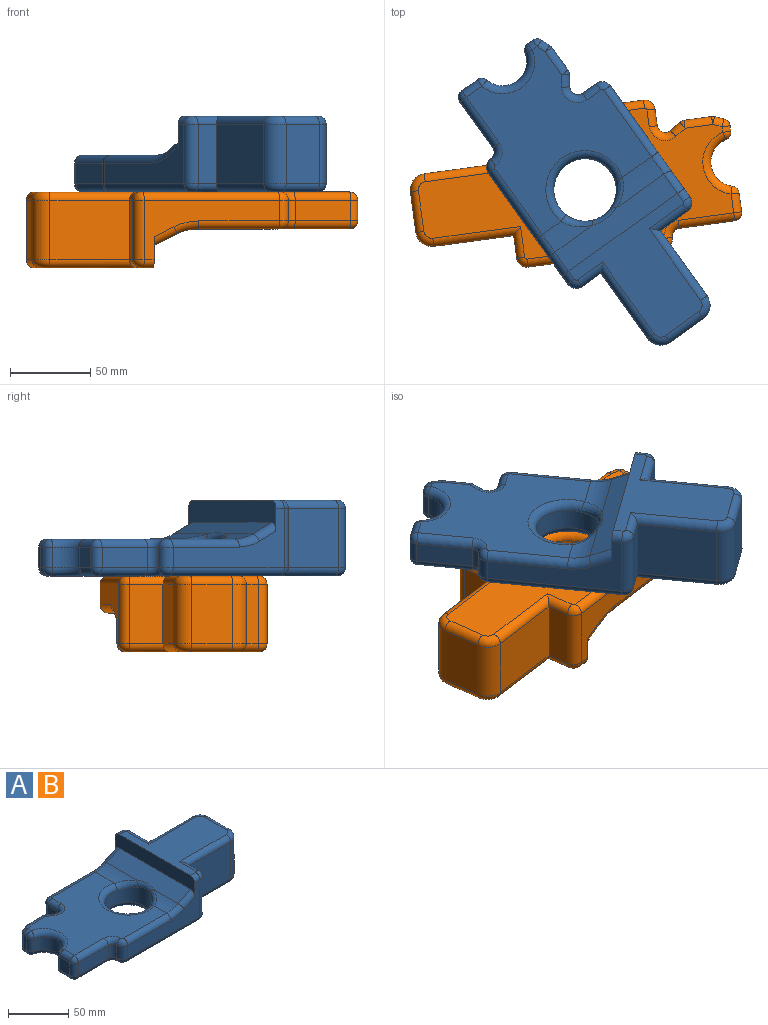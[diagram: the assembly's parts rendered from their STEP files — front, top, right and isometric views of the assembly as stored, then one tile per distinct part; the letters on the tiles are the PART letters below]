
ASSEMBLY  parts=2 mates=1
PART A: 109 faces, bbox 203.6x93.4x47.3 mm
  f0: cylinder r=30mm len=36.62mm, axis (0,-1,0), area 377.4mm2, adj f26,f28,f30,f66
  f1: cylinder r=30mm len=28.88mm, axis (0,-1,0), area 270.5mm2, adj f26,f28,f33,f44
  f2: plane 37.3x14.28mm, normal (1,0,0), area 532.7mm2, adj f3,f23,f76,f98
  f3: plane 50.1x37.3mm, normal (0,-1,0), area 1868.8mm2, adj f2,f4,f78,f96
  f4: cylinder r=10mm len=37.3mm, axis (0,0,-1), area 585.9mm2, adj f3,f5,f77,f94
  f5: plane 37.3x25.56mm, normal (1,0,0), area 953.5mm2, adj f4,f6,f75,f92
  f6: cylinder r=10mm len=37.3mm, axis (0,0,-1), area 585.9mm2, adj f5,f7,f73,f90
  f7: plane 50.1x37.3mm, normal (0,1,0), area 1868.8mm2, adj f6,f8,f71,f88
  f8: plane 37.3x20.87mm, normal (1,0,0), area 778.6mm2, adj f7,f9,f70,f86
  f9: cylinder r=6.35mm len=37.3mm, axis (0,0,-1), area 372.1mm2, adj f8,f10,f69,f84
  f10: plane 85.02x37.3mm, normal (0,1,0), area 1363.6mm2, adj f9,f11,f27,f65,f66,f67,f68,f82
  f11: cylinder r=6.35mm len=13.05mm, axis (0,0,-1), area 130.1mm2, adj f10,f12,f64,f80
  f12: plane 13.05x10.53mm, normal (-1,0,0), area 137.3mm2, adj f11,f35,f63,f79
  f13: plane 13.05x6.37mm, normal (0.57,0.82,0), area 100.7mm2, adj f35,f40,f61,f83
  f14: plane 17.3x13.05mm, normal (0,1,0), area 225.7mm2, adj f40,f41,f59,f87
  f15: plane 13.05x5.67mm, normal (-0.36,0.93,0), area 79.1mm2, adj f41,f42,f57,f91
  f16: plane 13.05x3.52mm, normal (-1,0,0), area 45.9mm2, adj f37,f42,f55,f95
  f17: cylinder r=15.04mm len=29.12mm, axis (0,0,-1), area 517.2mm2, adj f37,f38,f53,f99
  f18: plane 13.05x11.79mm, normal (-1,0,0), area 153.8mm2, adj f38,f39,f51,f103
  f19: plane 34.99x13.05mm, normal (0,-1,0), area 456.4mm2, adj f36,f39,f49,f107
  f20: plane 13.05x0.03mm, normal (-1,0,0), area 0.4mm2, adj f21,f36,f47,f106
  f21: cylinder r=6.35mm len=13.05mm, axis (0,0,-1), area 130.1mm2, adj f20,f22,f46,f104
  f22: plane 85.02x37.3mm, normal (0,-1,0), area 1363.6mm2, adj f21,f23,f27,f43,f44,f45,f72,f102
  f23: cylinder r=6.35mm len=37.3mm, axis (0,0,-1), area 372.1mm2, adj f2,f22,f74,f100
  f24: plane 83.42x67.73mm, normal (0,0,1), area 2762.3mm2, adj f27,f68,f69,f70,f71,f72,f73,f74
  f25: plane 192.81x83.42mm, normal (0,0,-1), area 9588.8mm2, adj f34,f79,f80,f81,f82,f83,f84,f86
  f26: plane 83.42x14.66mm, normal (-0.44,0,0.9), area 1342.7mm2, adj f0,f1,f27,f32,f43,f67
  f27: plane 93.42x19.43mm, normal (-1,0,0), area 1295.1mm2, adj f10,f22,f24,f26,f43,f67,f68,f72
  f28: plane 97.08x83.42mm, normal (0,0,1), area 5083.9mm2, adj f0,f1,f31,f45,f46,f47,f48,f49
  f29: cylinder r=19.49mm len=38.98mm, axis (0,0,-1), area 1710.3mm2, adj f30,f31,f32,f33,f34
  f30: bspline ~18.56x17.26mm, area 127.5mm2, adj f0,f29,f31,f32
  f31: torus R=24.49mm, axis (0,0,-1), area 625.9mm2, adj f28,f29,f30,f33
  f32: bspline ~17.93x5.32mm, area 91.8mm2, adj f26,f29,f30,f33
  f33: bspline ~18.06x17.1mm, area 127.5mm2, adj f1,f29,f31,f32
  f34: torus R=24.49mm, axis (0,0,1), area 1051.3mm2, adj f25,f29
  f35: cylinder r=5mm len=13.05mm, axis (0,0,1), area 141.6mm2, adj f12,f13,f62,f81
  f36: cylinder r=5mm len=13.05mm, axis (0,0,1), area 102.5mm2, adj f19,f20,f48,f108
  f37: cylinder r=5mm len=13.05mm, axis (0,0,-1), area 86mm2, adj f16,f17,f54,f97
  f38: cylinder r=5mm len=13.05mm, axis (0,0,-1), area 86mm2, adj f17,f18,f52,f101
  f39: cylinder r=5mm len=13.05mm, axis (0,0,-1), area 102.5mm2, adj f18,f19,f50,f105
  f40: cylinder r=5mm len=13.05mm, axis (0,0,-1), area 39.2mm2, adj f13,f14,f60,f85
  f41: cylinder r=5mm len=13.05mm, axis (0,0,-1), area 23.8mm2, adj f14,f15,f58,f89
  f42: cylinder r=5mm len=13.05mm, axis (0,0,-1), area 78.6mm2, adj f15,f16,f56,f93
  f43: cylinder r=5mm len=16.89mm, axis (-0.9,0,-0.44), area 121.5mm2, adj f22,f26,f27,f44
  f44: torus R=35mm, axis (0,1,0), area 115.1mm2, adj f1,f22,f43,f45
  f45: cylinder r=5mm len=50.74mm, axis (-1,0,0), area 398.5mm2, adj f22,f28,f44,f46
  f46: torus R=1.35mm, axis (0,0,-1), area 55.9mm2, adj f21,f28,f45,f47
  f47: cylinder r=5mm len=5mm, axis (0,1,0), area 0.2mm2, adj f20,f28,f46,f48
  f48: torus R=10mm, axis (0,0,-1), area 84.1mm2, adj f28,f36,f47,f49
  f49: cylinder r=5mm len=34.99mm, axis (-1,0,0), area 274.8mm2, adj f19,f28,f48,f50
  f50: sphere r=5mm, area 39.3mm2, adj f39,f49,f51
  f51: cylinder r=5mm len=11.79mm, axis (0,1,0), area 92.6mm2, adj f18,f28,f50,f52
  f52: sphere r=5mm, area 33mm2, adj f38,f51,f53
  f53: torus R=20.04mm, axis (0,0,-1), area 349.1mm2, adj f17,f28,f52,f54
  f54: sphere r=5mm, area 33mm2, adj f37,f53,f55
  f55: cylinder r=5mm len=5mm, axis (0,1,0), area 27.7mm2, adj f16,f28,f54,f56
  f56: sphere r=5mm, area 30.1mm2, adj f42,f55,f57
  f57: cylinder r=5mm len=7.45mm, axis (0.93,0.36,0), area 47.6mm2, adj f15,f28,f56,f58
  f58: sphere r=5mm, area 9.1mm2, adj f41,f57,f59
  f59: cylinder r=5mm len=17.3mm, axis (1,0,0), area 135.9mm2, adj f14,f28,f58,f60
  f60: sphere r=5mm, area 15mm2, adj f40,f59,f61
  f61: cylinder r=5mm len=9.2mm, axis (0.82,-0.57,0), area 60.7mm2, adj f13,f28,f60,f62
  f62: torus R=10mm, axis (0,0,-1), area 116.3mm2, adj f28,f35,f61,f63
  f63: cylinder r=5mm len=10.53mm, axis (0,1,0), area 82.7mm2, adj f12,f28,f62,f64
  f64: torus R=1.35mm, axis (0,0,-1), area 55.9mm2, adj f11,f28,f63,f65
  f65: cylinder r=5mm len=50.74mm, axis (1,0,0), area 398.5mm2, adj f10,f28,f64,f66
  f66: torus R=35mm, axis (0,1,0), area 115.1mm2, adj f0,f10,f65,f67
  f67: cylinder r=5mm len=16.89mm, axis (0.9,0,0.44), area 121.5mm2, adj f10,f26,f27,f66
  f68: cylinder r=5mm len=6.28mm, axis (1,0,0), area 49.3mm2, adj f10,f24,f27,f69
  f69: torus R=1.35mm, axis (0,0,1), area 55.9mm2, adj f9,f24,f68,f70
  f70: cylinder r=5mm len=25.87mm, axis (0,-1,0), area 178.2mm2, adj f8,f24,f69,f71
  f71: cylinder r=5mm len=55.1mm, axis (1,0,0), area 407.8mm2, adj f7,f24,f70,f73
  f72: cylinder r=5mm len=6.28mm, axis (-1,0,0), area 49.3mm2, adj f22,f24,f27,f74
  f73: torus R=5mm, axis (0,0,1), area 101mm2, adj f6,f24,f71,f75
  f74: torus R=1.35mm, axis (0,0,1), area 55.9mm2, adj f23,f24,f72,f76
  f75: cylinder r=5mm len=25.56mm, axis (0,-1,0), area 200.8mm2, adj f5,f24,f73,f77
  f76: cylinder r=5mm len=19.28mm, axis (0,-1,0), area 126.4mm2, adj f2,f24,f74,f78
  f77: torus R=5mm, axis (0,0,1), area 101mm2, adj f4,f24,f75,f78
  f78: cylinder r=5mm len=55.1mm, axis (-1,0,0), area 407.8mm2, adj f3,f24,f76,f77
  f79: cylinder r=5mm len=10.53mm, axis (0,-1,0), area 82.7mm2, adj f12,f25,f80,f81
  f80: torus R=1.35mm, axis (0,0,1), area 55.9mm2, adj f11,f25,f79,f82
  f81: torus R=10mm, axis (0,0,1), area 116.3mm2, adj f25,f35,f79,f83
  f82: cylinder r=5mm len=85.02mm, axis (-1,0,0), area 667.7mm2, adj f10,f25,f80,f84
  f83: cylinder r=5mm len=9.2mm, axis (-0.82,0.57,0), area 60.7mm2, adj f13,f25,f81,f85
  f84: torus R=1.35mm, axis (0,0,1), area 55.9mm2, adj f9,f25,f82,f86
  f85: sphere r=5mm, area 15mm2, adj f40,f83,f87
  f86: cylinder r=5mm len=25.87mm, axis (0,1,0), area 178.2mm2, adj f8,f25,f84,f88
  f87: cylinder r=5mm len=17.3mm, axis (-1,0,0), area 135.9mm2, adj f14,f25,f85,f89
  f88: cylinder r=5mm len=55.1mm, axis (-1,0,0), area 407.8mm2, adj f7,f25,f86,f90
  f89: sphere r=5mm, area 9.1mm2, adj f41,f87,f91
  f90: torus R=5mm, axis (0,0,1), area 101mm2, adj f6,f25,f88,f92
  f91: cylinder r=5mm len=7.45mm, axis (-0.93,-0.36,0), area 47.6mm2, adj f15,f25,f89,f93
  f92: cylinder r=5mm len=25.56mm, axis (0,1,0), area 200.8mm2, adj f5,f25,f90,f94
  f93: sphere r=5mm, area 30.1mm2, adj f42,f91,f95
  f94: torus R=5mm, axis (0,0,1), area 101mm2, adj f4,f25,f92,f96
  f95: cylinder r=5mm len=5mm, axis (0,-1,0), area 27.7mm2, adj f16,f25,f93,f97
  f96: cylinder r=5mm len=55.1mm, axis (1,0,0), area 407.8mm2, adj f3,f25,f94,f98
  f97: sphere r=5mm, area 33mm2, adj f37,f95,f99
  f98: cylinder r=5mm len=19.28mm, axis (0,1,0), area 126.4mm2, adj f2,f25,f96,f100
  f99: torus R=20.04mm, axis (0,0,1), area 349.1mm2, adj f17,f25,f97,f101
  f100: torus R=1.35mm, axis (0,0,1), area 55.9mm2, adj f23,f25,f98,f102
  f101: sphere r=5mm, area 33mm2, adj f38,f99,f103
  f102: cylinder r=5mm len=85.02mm, axis (1,0,0), area 667.7mm2, adj f22,f25,f100,f104
  f103: cylinder r=5mm len=11.79mm, axis (0,-1,0), area 92.6mm2, adj f18,f25,f101,f105
  f104: torus R=1.35mm, axis (0,0,1), area 55.9mm2, adj f21,f25,f102,f106
  f105: sphere r=5mm, area 39.3mm2, adj f39,f103,f107
  f106: cylinder r=5mm len=5mm, axis (0,-1,0), area 0.2mm2, adj f20,f25,f104,f108
  f107: cylinder r=5mm len=34.99mm, axis (1,0,0), area 274.8mm2, adj f19,f25,f105,f108
  f108: torus R=10mm, axis (0,0,1), area 84.1mm2, adj f25,f36,f106,f107
PART B: same geometry as A
PLACE A rot(axis=(0,0,-1),54.4deg) t=(-4.67,240.15,190.53)mm
PLACE B rot(axis=(-0.07,1,0),180deg) t=(-4.67,240.15,190.53)mm
MATE revolute B.f29 <-> A.f29  axis (0,0,1) through (-4.67,240.15,190.53)mm
